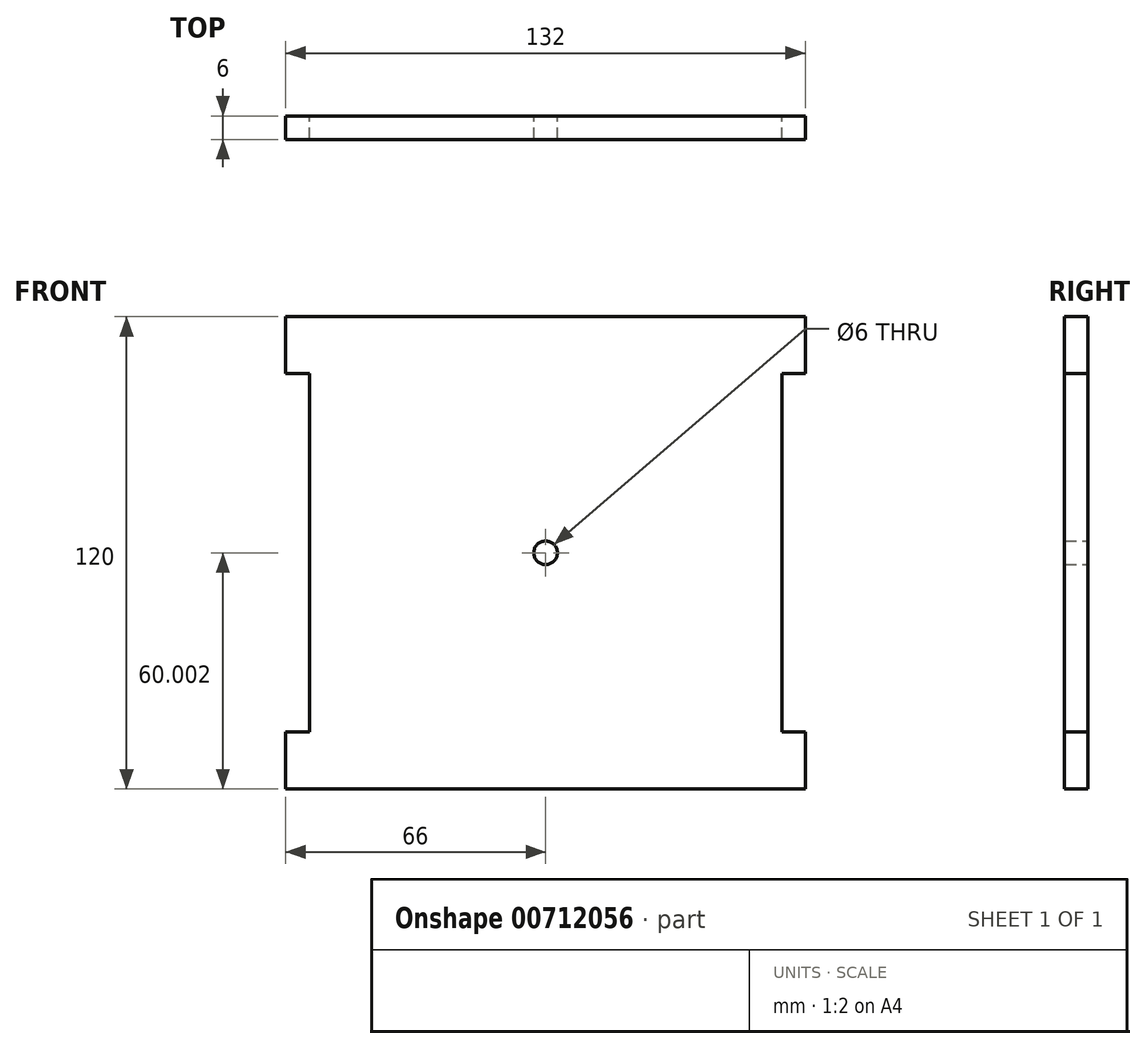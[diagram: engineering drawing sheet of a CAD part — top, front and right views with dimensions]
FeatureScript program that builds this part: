
annotation { "Feature Type Name" : "Feature", "Feature Type Description" : "" }
export const myFeature = defineFeature(function(context is Context, id is Id, definition is map)
    precondition{}
    {
        {
            var Q0;
            Q0=qCreatedBy(makeId("Front.planeOp"),FACE);
            var sketch = newSketch(context, id + "F0", { "sketchPlane" : qUnion([Q0])});
            skLineSegment(sketch, "E0", {"start": v(-132, 42.03) * mm, "end": v(0, 42.03) * mm});
            skLineSegment(sketch, "E1", {"start": v(-132, 42.03) * mm, "end": v(-132, 27.53) * mm});
            skLineSegment(sketch, "E2", {"start": v(-132, 27.53) * mm, "end": v(-126, 27.53) * mm});
            skLineSegment(sketch, "E3", {"start": v(-126, 27.53) * mm, "end": v(-126, -63.47) * mm});
            skLineSegment(sketch, "E4", {"start": v(-126, -63.47) * mm, "end": v(-132, -63.47) * mm});
            skLineSegment(sketch, "E5", {"start": v(-132, -63.47) * mm, "end": v(-132, -77.97) * mm});
            skLineSegment(sketch, "E6", {"start": v(-132, -77.97) * mm, "end": v(0, -77.97) * mm});
            skLineSegment(sketch, "E7", {"start": v(0, -77.97) * mm, "end": v(0, -63.47) * mm});
            skLineSegment(sketch, "E8", {"start": v(0, -63.47) * mm, "end": v(-6, -63.47) * mm});
            skLineSegment(sketch, "E9", {"start": v(-6, -63.47) * mm, "end": v(-6, 27.53) * mm});
            skLineSegment(sketch, "E10", {"start": v(-6, 27.53) * mm, "end": v(0, 27.53) * mm});
            skLineSegment(sketch, "E11", {"start": v(0, 27.53) * mm, "end": v(0, 42.03) * mm});
            skCircle(sketch, "E12", {"center": v(-66, -17.97) * mm, "radius": 3 * mm});
            skSolve(sketch);
        }
        {
            var Q0;
            Q0=makeQuery(id+"F0.imprint","IMPRINT",FACE,{"disambiguationData":[TD([[makeQuery(id+"F0.imprint","IMPRINT",EDGE,{"derivedFrom":sQuery(id+"F0.wireOp",EDGE,"E0")}),-1.0]])]});
            extrude(context, id + "F1", {"entities" : qUnion([Q0]), "depth" : 6 * mm, "offsetDistance" : 25 * mm});
        }
    });
